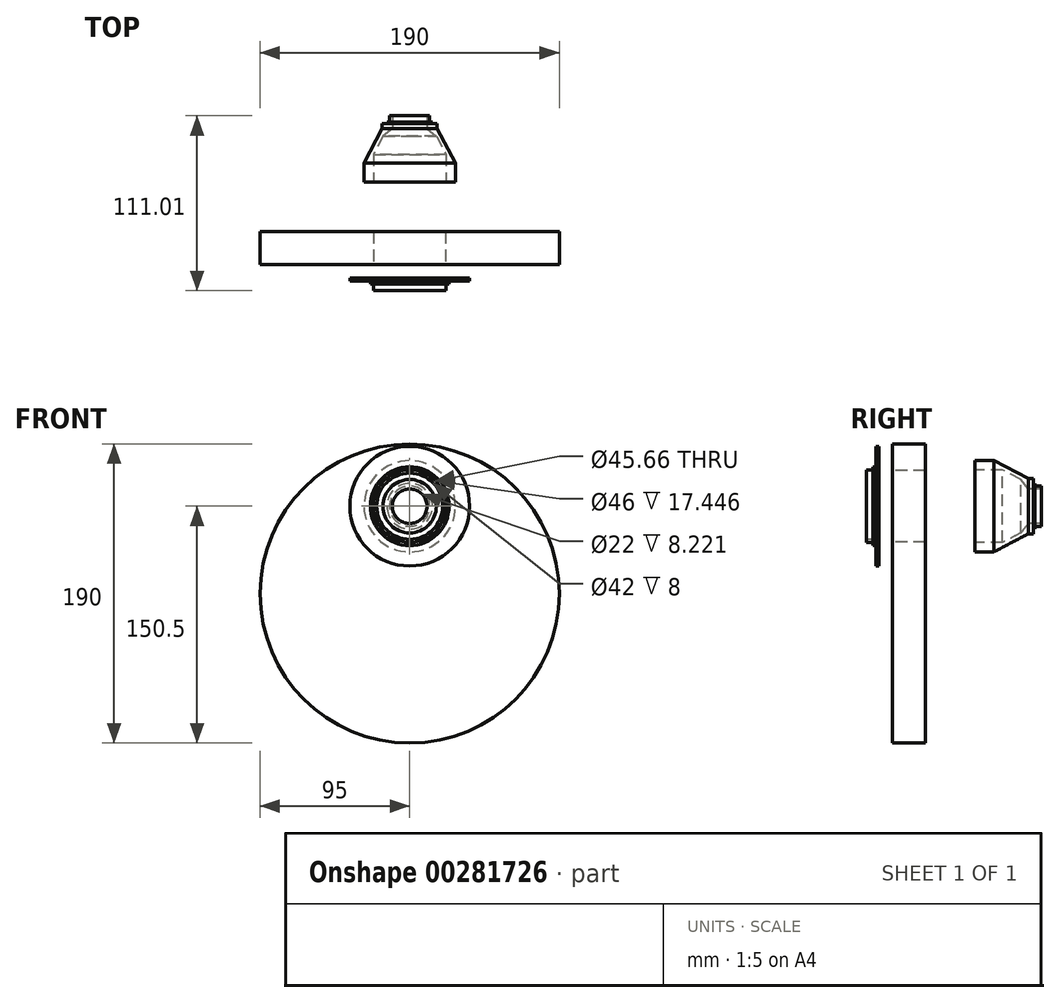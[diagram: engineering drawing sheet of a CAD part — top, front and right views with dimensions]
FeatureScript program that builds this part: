
annotation { "Feature Type Name" : "Feature", "Feature Type Description" : "" }
export const myFeature = defineFeature(function(context is Context, id is Id, definition is map)
    precondition{}
    {
        {
            var Q0;
            Q0=qCreatedBy(makeId("Right.planeOp"),FACE);
            var sketch = newSketch(context, id + "F0", { "sketchPlane" : qUnion([Q0])});
            skLineSegment(sketch, "E0", {"start": v(0, 21) * mm, "end": v(0, 38) * mm});
            skLineSegment(sketch, "E1", {"start": v(0, 38) * mm, "end": v(-2, 38) * mm});
            skLineSegment(sketch, "E2", {"start": v(-2, 38) * mm, "end": v(-2, 25) * mm});
            skLineSegment(sketch, "E3", {"start": v(-2, 25) * mm, "end": v(-4, 25) * mm});
            skLineSegment(sketch, "E4", {"start": v(-4, 25) * mm, "end": v(-4, 23) * mm});
            skLineSegment(sketch, "E5", {"start": v(-4, 23) * mm, "end": v(-8, 23) * mm});
            skLineSegment(sketch, "E6", {"start": v(-8, 23) * mm, "end": v(-8, 21) * mm});
            skLineSegment(sketch, "E7", {"start": v(-8, 21) * mm, "end": v(0, 21) * mm});
            skLineSegment(sketch, "E8", {"start": v(-33.33, 0) * mm, "end": v(12.74, 0) * mm, "construction": true});
            skLineSegment(sketch, "E9", {"start": v(-35.6, -55.5) * mm, "end": v(68.32, -55.5) * mm, "construction": true});
            skLineSegment(sketch, "E10", {"start": v(8.47, 39.5) * mm, "end": v(29.47, 39.5) * mm});
            skLineSegment(sketch, "E11", {"start": v(8.47, 39.5) * mm, "end": v(8.47, -55.5) * mm});
            skLineSegment(sketch, "E12", {"start": v(29.47, 39.5) * mm, "end": v(29.47, -55.5) * mm});
            skLineSegment(sketch, "E13", {"start": v(8.47, -55.5) * mm, "end": v(29.47, -55.5) * mm});
            skLineSegment(sketch, "E14", {"start": v(61.01, 23) * mm, "end": v(61.01, 29) * mm});
            skLineSegment(sketch, "E15", {"start": v(61.01, 29) * mm, "end": v(73.01, 29) * mm});
            skLineSegment(sketch, "E16", {"start": v(73.01, 29) * mm, "end": v(95.01, 17.5) * mm});
            skLineSegment(sketch, "E17", {"start": v(95.01, 17.5) * mm, "end": v(98.01, 17.5) * mm});
            skLineSegment(sketch, "E18", {"start": v(98.01, 17.5) * mm, "end": v(98.01, 14.5) * mm});
            skLineSegment(sketch, "E19", {"start": v(98.01, 14.5) * mm, "end": v(99.01, 14.5) * mm});
            skLineSegment(sketch, "E20", {"start": v(99.01, 14.5) * mm, "end": v(99.01, 12.75) * mm});
            skLineSegment(sketch, "E21", {"start": v(99.01, 12.75) * mm, "end": v(103.01, 12.75) * mm});
            skLineSegment(sketch, "E22", {"start": v(103.01, 12.75) * mm, "end": v(103.01, 11) * mm});
            skLineSegment(sketch, "E23", {"start": v(103.01, 11) * mm, "end": v(94.8, 11) * mm});
            skPoint(sketch, "E24.orphan", {"position": v(61.01, 0) * mm});
            skPoint(sketch, "E25.orphan", {"position": v(103.01, 0) * mm});
            skLineSegment(sketch, "E26", {"start": v(61.01, 23) * mm, "end": v(78.46, 23) * mm});
            skLineSegment(sketch, "E27", {"start": v(78.46, 23) * mm, "end": v(90.08, 16.93) * mm});
            skLineSegment(sketch, "E28", {"start": v(90.08, 16.93) * mm, "end": v(94.8, 11) * mm});
            skSolve(sketch);
        }
        {
            var Q0;
            Q0=makeQuery(id+"F0.imprint","IMPRINT",FACE,{"disambiguationData":[TD([[makeQuery(id+"F0.imprint","IMPRINT",EDGE,{"derivedFrom":sQuery(id+"F0.wireOp",EDGE,"E0")}),1.0]])]});
            var Q1;
            Q1=sQuery(id+"F0.wireOp",EDGE,"E8");
            revolve(context, id + "F1", {"surfaceOperationType" : NewSurfaceOperationType.NEW, "entities" : qUnion([Q0]), "axis" : qUnion([Q1]), "revolveType" : RevolveType.FULL});
        }
        {
            var Q0;
            Q0=makeQuery(id+"F0.imprint","IMPRINT",FACE,{"disambiguationData":[TD([[makeQuery(id+"F0.imprint","IMPRINT",EDGE,{"derivedFrom":sQuery(id+"F0.wireOp",EDGE,"E10")}),-1.0]])]});
            var Q1;
            Q1=sQuery(id+"F0.wireOp",EDGE,"E9");
            revolve(context, id + "F2", {"surfaceOperationType" : NewSurfaceOperationType.NEW, "entities" : qUnion([Q0]), "axis" : qUnion([Q1]), "revolveType" : RevolveType.FULL});
        }
        {
            var Q0;
            Q0=makeQuery(id+"F2.opRevolve","SWEPT_FACE",FACE,{"disambiguationData":[OSD([sQuery(id+"F0.wireOp",EDGE,"E11")])]});
            var sketch = newSketch(context, id + "F3", { "sketchPlane" : qUnion([Q0])});
            skCircle(sketch, "E29", {"center": v(0, 0) * mm, "radius": 22.83 * mm});
            skSolve(sketch);
        }
        {
            var Q0;
            Q0 = qSketchRegion(id + "F3", true);
            extrude(context, id + "F4", {"entities" : qUnion([Q0]), "operationType" : NewBodyOperationType.REMOVE, "oppositeDirection" : true, "depth" : 25 * mm, "offsetDistance" : 25 * mm});
        }
        {
            var Q0;
            Q0=makeQuery(id+"F0.imprint","IMPRINT",FACE,{"disambiguationData":[TD([[makeQuery(id+"F0.imprint","IMPRINT",EDGE,{"derivedFrom":sQuery(id+"F0.wireOp",EDGE,"E14")}),-1.0]])]});
            var Q1;
            Q1=sQuery(id+"F0.wireOp",EDGE,"E8");
            revolve(context, id + "F5", {"surfaceOperationType" : NewSurfaceOperationType.NEW, "entities" : qUnion([Q0]), "axis" : qUnion([Q1]), "revolveType" : RevolveType.FULL});
        }
    });
